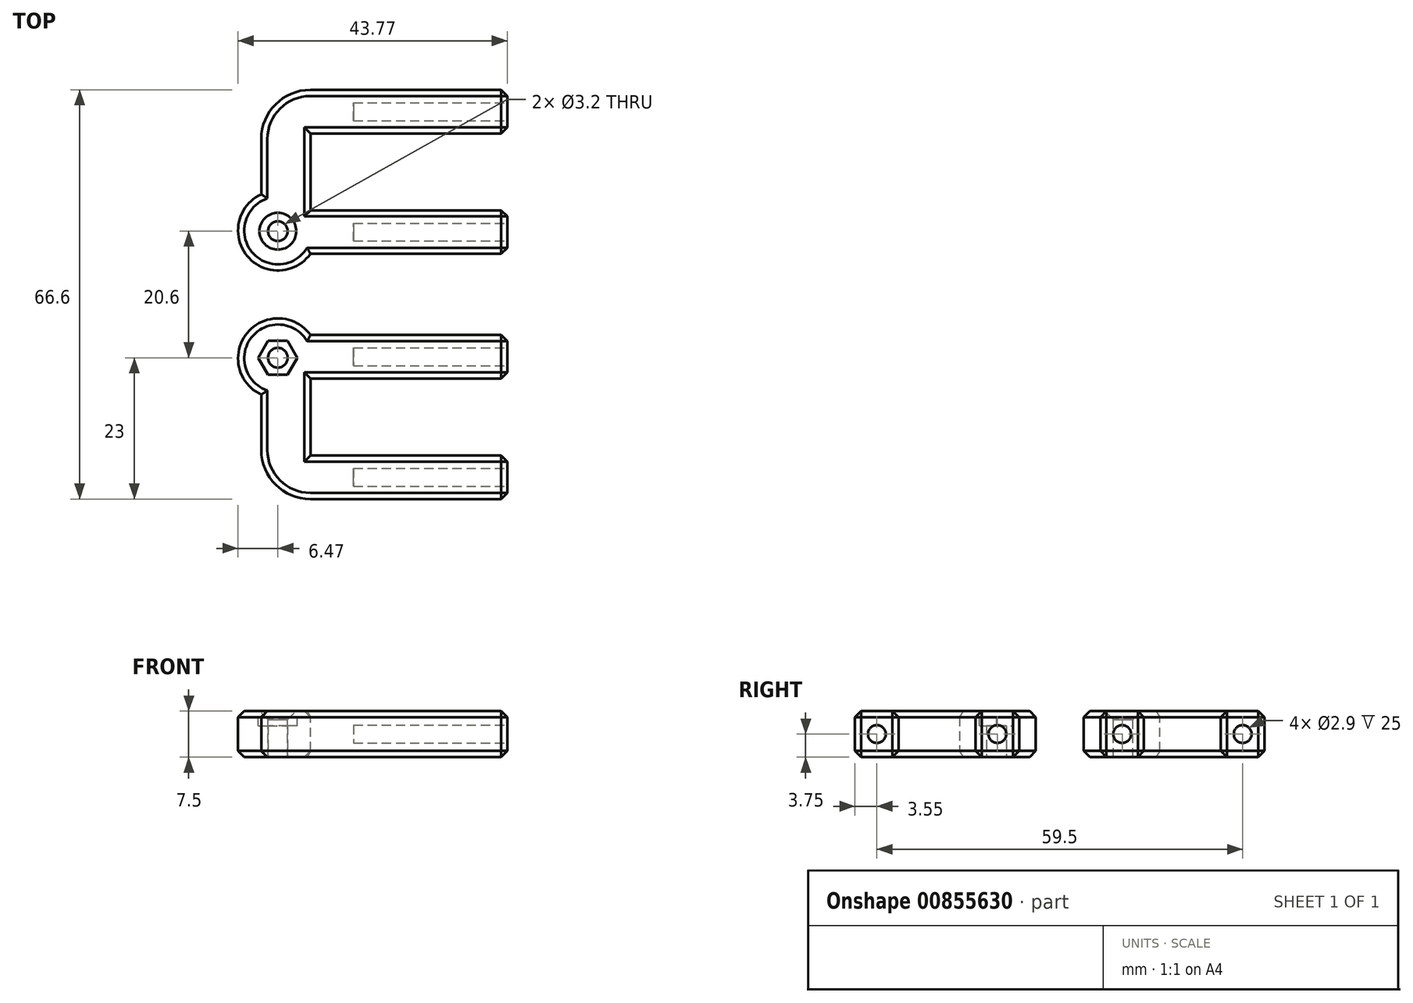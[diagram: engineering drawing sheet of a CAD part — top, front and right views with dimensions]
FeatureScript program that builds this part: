
annotation { "Feature Type Name" : "Feature", "Feature Type Description" : "" }
export const myFeature = defineFeature(function(context is Context, id is Id, definition is map)
    precondition{}
    {
        {
            var Q0;
            Q0=qCreatedBy(makeId("Top.planeOp"),FACE);
            var sketch = newSketch(context, id + "F0", { "sketchPlane" : qUnion([Q0])});
            skLineSegment(sketch, "E0", {"start": v(0, 0) * mm, "end": v(0, 7.1) * mm});
            skLineSegment(sketch, "E1", {"start": v(0, 7.1) * mm, "end": v(-32, 7.1) * mm});
            skLineSegment(sketch, "E2", {"start": v(-32, 7.1) * mm, "end": v(-32, 19.6) * mm});
            skLineSegment(sketch, "E3", {"start": v(-32, 19.6) * mm, "end": v(0, 19.6) * mm});
            skLineSegment(sketch, "E4", {"start": v(0, 19.6) * mm, "end": v(0, 26.7) * mm});
            skLineSegment(sketch, "E5", {"start": v(0, 26.7) * mm, "end": v(-32, 26.7) * mm});
            skLineSegment(sketch, "E6", {"start": v(0, 0) * mm, "end": v(-32, 0) * mm});
            skArc(sketch, "E7", {"start": v(-40, 8) * mm, "mid": v(-37.66, 2.34) * mm, "end": v(-32, 0) * mm});
            skLineSegment(sketch, "E8", {"start": v(-40, 8) * mm, "end": v(-40, 17) * mm});
            skCircle(sketch, "E9", {"center": v(-37.3, 23) * mm, "radius": 1.6 * mm});
            skArc(sketch, "E10", {"start": v(-32, 26.7) * mm, "mid": v(-42.29, 27.04) * mm, "end": v(-40, 17) * mm});
            skSolve(sketch);
        }
        {
            var Q0;
            Q0=makeQuery(id+"F0.imprint","IMPRINT",FACE,{"disambiguationData":[TD([[makeQuery(id+"F0.imprint","IMPRINT",EDGE,{"derivedFrom":sQuery(id+"F0.wireOp",EDGE,"E0")}),1.0]])]});
            extrude(context, id + "F1", {"entities" : qUnion([Q0]), "depth" : 7.5 * mm, "offsetDistance" : 25 * mm});
        }
        {
            var Q0;
            Q0=makeQuery(id+"F1.opExtrude","SWEPT_FACE",FACE,{"disambiguationData":[OSD([sQuery(id+"F0.wireOp",EDGE,"E4")])]});
            var sketch = newSketch(context, id + "F2", { "sketchPlane" : qUnion([Q0])});
            skPoint(sketch, "E11.0", {"position": v(0, 3.75) * mm});
            skPoint(sketch, "E12.0", {"position": v(3.55, 7.5) * mm});
            skPoint(sketch, "E13.0", {"position": v(23.15, 7.5) * mm});
            skPoint(sketch, "E14.0", {"position": v(26.7, 3.75) * mm});
            skCircle(sketch, "E15", {"center": v(3.55, 3.75) * mm, "radius": 1.45 * mm});
            skCircle(sketch, "E16", {"center": v(23.15, 3.75) * mm, "radius": 1.45 * mm});
            skSolve(sketch);
        }
        {
            var Q0;
            Q0=makeQuery(id+"F2.imprint","IMPRINT",FACE,{"disambiguationData":[TD([[makeQuery(id+"F2.imprint","IMPRINT",EDGE,{"derivedFrom":sQuery(id+"F2.wireOp",EDGE,"E15")}),1.0]])]});
            var Q1;
            Q1=makeQuery(id+"F2.imprint","IMPRINT",FACE,{"disambiguationData":[TD([[makeQuery(id+"F2.imprint","IMPRINT",EDGE,{"derivedFrom":sQuery(id+"F2.wireOp",EDGE,"E16")}),1.0]])]});
            extrude(context, id + "F3", {"entities" : qUnion([Q0, Q1]), "operationType" : NewBodyOperationType.REMOVE, "oppositeDirection" : true, "depth" : 25 * mm, "offsetDistance" : 25 * mm});
        }
        {
            var Q0;
            Q0=makeQuery(id+"F1.opExtrude","CAP_EDGE",EDGE,{"disambiguationData":[OSD([sQuery(id+"F0.wireOp",EDGE,"E6")])],"isStart":false});
            var Q1;
            Q1=makeQuery(id+"F1.opExtrude","CAP_EDGE",EDGE,{"disambiguationData":[OSD([sQuery(id+"F0.wireOp",EDGE,"E6")])],"isStart":true});
            var Q2;
            Q2=makeQuery(id+"F1.opExtrude","CAP_EDGE",EDGE,{"disambiguationData":[OSD([sQuery(id+"F0.wireOp",EDGE,"E1")])],"isStart":false});
            var Q3;
            Q3=makeQuery(id+"F1.opExtrude","CAP_EDGE",EDGE,{"disambiguationData":[OSD([sQuery(id+"F0.wireOp",EDGE,"E1")])],"isStart":true});
            var Q4;
            Q4=makeQuery(id+"F1.opExtrude","CAP_EDGE",EDGE,{"disambiguationData":[OSD([sQuery(id+"F0.wireOp",EDGE,"E5")])],"isStart":true});
            var Q5;
            Q5=makeQuery(id+"F1.opExtrude","CAP_EDGE",EDGE,{"disambiguationData":[OSD([sQuery(id+"F0.wireOp",EDGE,"E5")])],"isStart":false});
            var Q6;
            Q6=makeQuery(id+"F1.opExtrude","CAP_EDGE",EDGE,{"disambiguationData":[OSD([sQuery(id+"F0.wireOp",EDGE,"E3")])],"isStart":false});
            var Q7;
            Q7=makeQuery(id+"F1.opExtrude","CAP_EDGE",EDGE,{"disambiguationData":[OSD([sQuery(id+"F0.wireOp",EDGE,"E3")])],"isStart":true});
            var Q8;
            Q8=makeQuery(id+"F1.opExtrude","CAP_EDGE",EDGE,{"disambiguationData":[OSD([sQuery(id+"F0.wireOp",EDGE,"E2")])],"isStart":true});
            var Q9;
            Q9=makeQuery(id+"F1.opExtrude","CAP_EDGE",EDGE,{"disambiguationData":[OSD([sQuery(id+"F0.wireOp",EDGE,"E2")])],"isStart":false});
            var Q10;
            Q10=makeQuery(id+"F1.opExtrude","CAP_EDGE",EDGE,{"disambiguationData":[OSD([sQuery(id+"F0.wireOp",EDGE,"E10")])],"isStart":true});
            var Q11;
            Q11=makeQuery(id+"F1.opExtrude","CAP_EDGE",EDGE,{"disambiguationData":[OSD([sQuery(id+"F0.wireOp",EDGE,"E10")])],"isStart":false});
            var Q12;
            Q12=makeQuery(id+"F1.opExtrude","SWEPT_EDGE",EDGE,{"disambiguationData":[OSD([sQuery(id+"F0.wireOp",EDGE,"E4"),sQuery(id+"F0.wireOp",EDGE,"E5")])]});
            var Q13;
            Q13=makeQuery(id+"F1.opExtrude","CAP_EDGE",EDGE,{"disambiguationData":[OSD([sQuery(id+"F0.wireOp",EDGE,"E4")])],"isStart":true});
            var Q14;
            Q14=makeQuery(id+"F1.opExtrude","SWEPT_EDGE",EDGE,{"disambiguationData":[OSD([sQuery(id+"F0.wireOp",EDGE,"E3"),sQuery(id+"F0.wireOp",EDGE,"E4")])]});
            var Q15;
            Q15=makeQuery(id+"F1.opExtrude","CAP_EDGE",EDGE,{"disambiguationData":[OSD([sQuery(id+"F0.wireOp",EDGE,"E4")])],"isStart":false});
            var Q16;
            Q16=makeQuery(id+"F1.opExtrude","CAP_EDGE",EDGE,{"disambiguationData":[OSD([sQuery(id+"F0.wireOp",EDGE,"E0")])],"isStart":false});
            var Q17;
            Q17=makeQuery(id+"F1.opExtrude","SWEPT_EDGE",EDGE,{"disambiguationData":[OSD([sQuery(id+"F0.wireOp",EDGE,"E0"),sQuery(id+"F0.wireOp",EDGE,"E1")])]});
            var Q18;
            Q18=makeQuery(id+"F1.opExtrude","CAP_EDGE",EDGE,{"disambiguationData":[OSD([sQuery(id+"F0.wireOp",EDGE,"E0")])],"isStart":true});
            var Q19;
            Q19=makeQuery(id+"F1.opExtrude","SWEPT_EDGE",EDGE,{"disambiguationData":[OSD([sQuery(id+"F0.wireOp",EDGE,"E0"),sQuery(id+"F0.wireOp",EDGE,"E6")])]});
            var Q20;
            Q20=makeQuery(id+"F3.boolean.opBoolean","COPY",EDGE,{"derivedFrom":makeQuery(id+"F3.opExtrude","CAP_EDGE",EDGE,{"disambiguationData":[OSD([sQuery(id+"F2.wireOp",EDGE,"E15")])],"isStart":true})});
            var Q21;
            Q21=makeQuery(id+"F3.boolean.opBoolean","COPY",EDGE,{"derivedFrom":makeQuery(id+"F3.opExtrude","CAP_EDGE",EDGE,{"disambiguationData":[OSD([sQuery(id+"F2.wireOp",EDGE,"E16")])],"isStart":true})});
            chamfer(context, id + "F4", {"entities" : qUnion([Q0, Q1, Q2, Q3, Q4, Q5, Q6, Q7, Q8, Q9, Q10, Q11, Q12, Q13, Q14, Q15, Q16, Q17, Q18, Q19, Q20, Q21]), "width" : 1 * mm, "tangentPropagation" : true});
        }
        {
            var Q0;
            Q0=makeQuery(id+"F1.opExtrude","SWEPT_BODY",BODY,{"disambiguationData":[OSD([sQuery(id+"F0.wireOp",EDGE,"E0"),sQuery(id+"F0.wireOp",EDGE,"E1"),sQuery(id+"F0.wireOp",EDGE,"E2"),sQuery(id+"F0.wireOp",EDGE,"E3"),sQuery(id+"F0.wireOp",EDGE,"E4"),sQuery(id+"F0.wireOp",EDGE,"E5"),sQuery(id+"F0.wireOp",EDGE,"E6"),sQuery(id+"F0.wireOp",EDGE,"E7"),sQuery(id+"F0.wireOp",EDGE,"E8"),sQuery(id+"F0.wireOp",EDGE,"E9"),sQuery(id+"F0.wireOp",EDGE,"E10")])]});
            transform(context, id + "F5", {"entities" : qUnion([Q0]), "transformType" : TransformType.TRANSLATION_3D, "dx" : 0 * mm, "dy" : 59.5 * mm, "dz" : 0 * mm, "makeCopy" : true});
        }
        {
            var Q0;
            Q0=makeQuery(id+"F5.opPattern","COPY",BODY,{"derivedFrom":makeQuery(id+"F1.opExtrude","SWEPT_BODY",BODY,{"disambiguationData":[OSD([sQuery(id+"F0.wireOp",EDGE,"E0"),sQuery(id+"F0.wireOp",EDGE,"E1"),sQuery(id+"F0.wireOp",EDGE,"E2"),sQuery(id+"F0.wireOp",EDGE,"E3"),sQuery(id+"F0.wireOp",EDGE,"E4"),sQuery(id+"F0.wireOp",EDGE,"E5"),sQuery(id+"F0.wireOp",EDGE,"E6"),sQuery(id+"F0.wireOp",EDGE,"E7"),sQuery(id+"F0.wireOp",EDGE,"E8"),sQuery(id+"F0.wireOp",EDGE,"E9"),sQuery(id+"F0.wireOp",EDGE,"E10")])]}),"instanceName":"1"});
            var Q1;
            Q1=makeQuery(id+"F5.opPattern","COPY",FACE,{"derivedFrom":makeQuery(id+"F3.boolean.opBoolean","COPY",FACE,{"derivedFrom":makeQuery(id+"F3.opExtrude","SWEPT_FACE",FACE,{"disambiguationData":[OSD([sQuery(id+"F2.wireOp",EDGE,"E15")])]})}),"instanceName":"1"});
            transform(context, id + "F6", {"entities" : qUnion([Q0]), "transformType" : TransformType.ROTATION, "transformAxis" : qUnion([Q1]), "angle" : 180 * degree, "makeCopy" : false});
        }
        {
            var Q0;
            Q0=makeQuery(id+"F1.opExtrude","CAP_FACE",FACE,{"disambiguationData":[OSD([sQuery(id+"F0.wireOp",EDGE,"E0"),sQuery(id+"F0.wireOp",EDGE,"E1"),sQuery(id+"F0.wireOp",EDGE,"E2"),sQuery(id+"F0.wireOp",EDGE,"E3"),sQuery(id+"F0.wireOp",EDGE,"E4"),sQuery(id+"F0.wireOp",EDGE,"E5"),sQuery(id+"F0.wireOp",EDGE,"E6"),sQuery(id+"F0.wireOp",EDGE,"E7"),sQuery(id+"F0.wireOp",EDGE,"E8"),sQuery(id+"F0.wireOp",EDGE,"E9"),sQuery(id+"F0.wireOp",EDGE,"E10")])],"isStart":false});
            var sketch = newSketch(context, id + "F7", { "sketchPlane" : qUnion([Q0])});
            skCircle(sketch, "E17.cCircle", {"center": v(-37.3, 23) * mm, "radius": 2.75 * mm, "construction": true});
            skLineSegment(sketch, "E17.0", {"start": v(-38.89, 25.75) * mm, "end": v(-35.71, 25.75) * mm});
            skLineSegment(sketch, "E17.1", {"start": v(-35.71, 25.75) * mm, "end": v(-34.12, 23) * mm});
            skLineSegment(sketch, "E17.2", {"start": v(-34.12, 23) * mm, "end": v(-35.71, 20.25) * mm});
            skLineSegment(sketch, "E17.3", {"start": v(-35.71, 20.25) * mm, "end": v(-38.89, 20.25) * mm});
            skLineSegment(sketch, "E17.4", {"start": v(-38.89, 20.25) * mm, "end": v(-40.48, 23) * mm});
            skLineSegment(sketch, "E17.5", {"start": v(-40.48, 23) * mm, "end": v(-38.89, 25.75) * mm});
            skPoint(sketch, "E17.0.midPoint", {"position": v(-37.3, 25.75) * mm});
            skSolve(sketch);
        }
        {
            var Q0;
            Q0=makeQuery(id+"F7.imprint","IMPRINT",FACE,{"disambiguationData":[TD([[makeQuery(id+"F7.imprint","IMPRINT",EDGE,{"derivedFrom":sQuery(id+"F7.wireOp",EDGE,"E17.0")}),-1.0]])]});
            extrude(context, id + "F8", {"entities" : qUnion([Q0]), "operationType" : NewBodyOperationType.REMOVE, "oppositeDirection" : true, "depth" : 2.4 * mm, "offsetDistance" : 25 * mm});
        }
        {
            var Q0;
            Q0=makeQuery(id+"F5.opPattern","COPY",EDGE,{"derivedFrom":makeQuery(id+"F1.opExtrude","CAP_EDGE",EDGE,{"disambiguationData":[OSD([sQuery(id+"F0.wireOp",EDGE,"E9")])],"isStart":true}),"instanceName":"1"});
            chamfer(context, id + "F9", {"entities" : qUnion([Q0]), "width" : 1.4 * mm, "tangentPropagation" : true});
        }
    });
